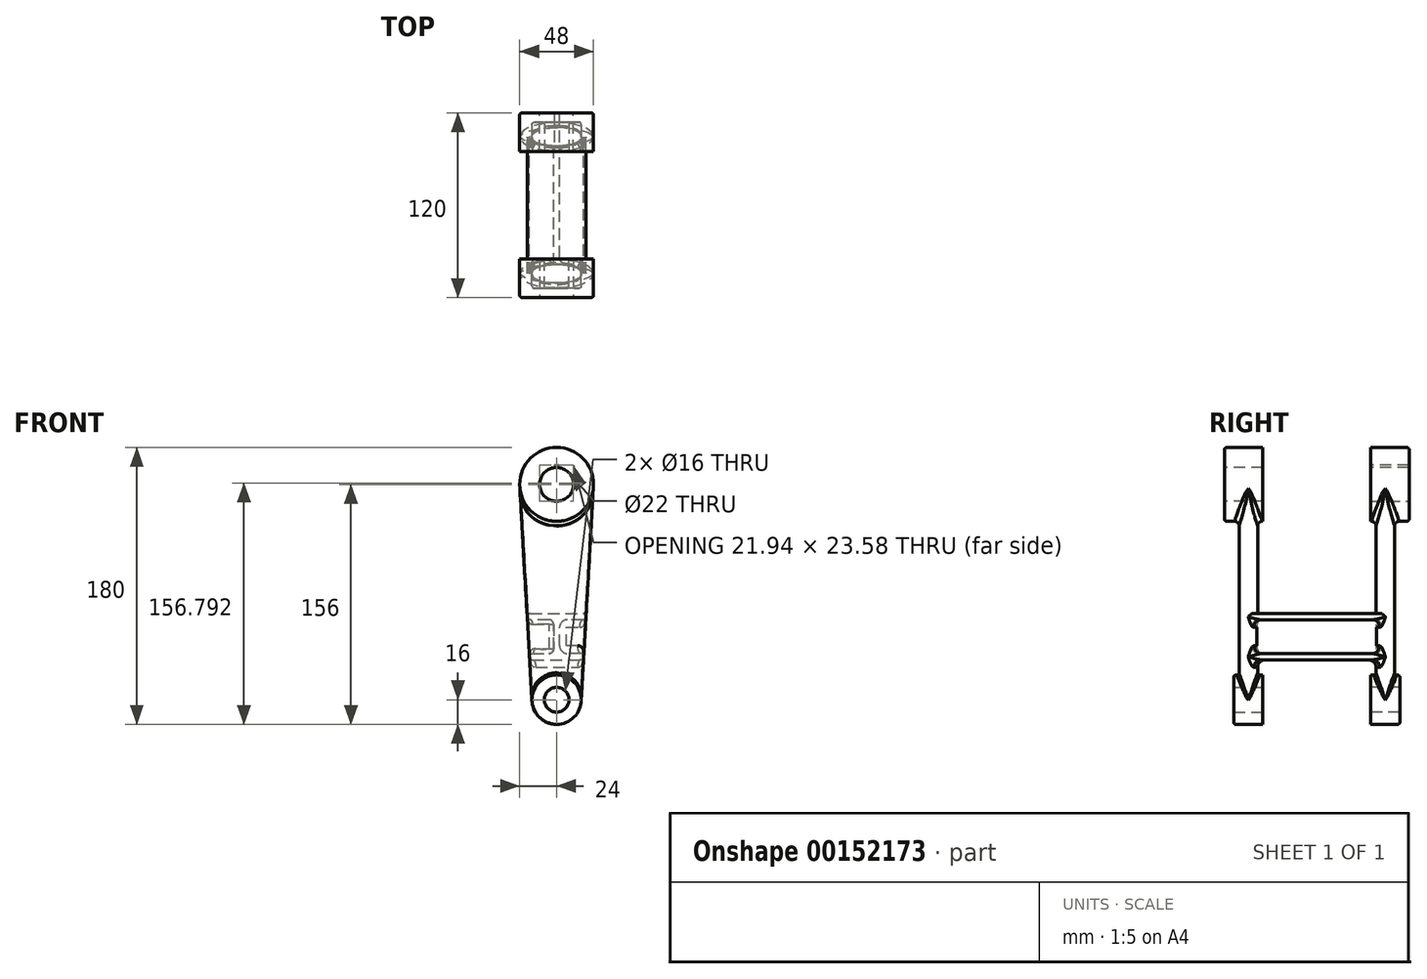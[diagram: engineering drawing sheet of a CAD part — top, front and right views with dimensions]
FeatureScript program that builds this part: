
annotation { "Feature Type Name" : "Feature", "Feature Type Description" : "" }
export const myFeature = defineFeature(function(context is Context, id is Id, definition is map)
    precondition{}
    {
        {
            var Q0;
            Q0=qCreatedBy(makeId("Front.planeOp"),FACE);
            var sketch = newSketch(context, id + "F0", { "sketchPlane" : qUnion([Q0])});
            skCircle(sketch, "E0", {"center": v(0, 140) * mm, "radius": 24 * mm});
            skCircle(sketch, "E1", {"center": v(0, 0) * mm, "radius": 16 * mm});
            skLineSegment(sketch, "E2", {"start": v(-16, 0) * mm, "end": v(-23.96, 138.62) * mm});
            skLineSegment(sketch, "E3", {"start": v(16, 0) * mm, "end": v(23.96, 138.62) * mm});
            skLineSegment(sketch, "E4", {"start": v(-23.96, 138.62) * mm, "end": v(23.96, 138.62) * mm, "construction": true});
            skSolve(sketch);
        }
        {
            var Q0;
            {var subQ0=sQuery(id+"F0.wireOp",EDGE,"E1");var subQ1=makeQuery(id+"F0.imprint","INTERSECT",VERTEX,{"derivedFrom":[subQ0,sQuery(id+"F0.wireOp",EDGE,"E2")]});Q0=makeQuery(id+"F0.imprint","IMPRINT",FACE,{"disambiguationData":[TD([[makeQuery(id+"F0.imprint","IMPRINT",EDGE,{"disambiguationData":[TD([[subQ1,1.0]])],"derivedFrom":subQ0}),1.0]])]});}
            extrude(context, id + "F1", {"entities" : qUnion([Q0]), "depth" : 19 * mm});
        }
        {
            var Q0;
            {var subQ0=sQuery(id+"F0.wireOp",EDGE,"E0");var subQ1=makeQuery(id+"F0.imprint","INTERSECT",VERTEX,{"derivedFrom":[subQ0,sQuery(id+"F0.wireOp",EDGE,"E2")]});Q0=makeQuery(id+"F0.imprint","IMPRINT",FACE,{"disambiguationData":[TD([[makeQuery(id+"F0.imprint","IMPRINT",EDGE,{"disambiguationData":[TD([[subQ1,-1.0]])],"derivedFrom":subQ0}),1.0]])]});}
            extrude(context, id + "F2", {"entities" : qUnion([Q0]), "depth" : 25 * mm});
        }
        {
            var Q0;
            Q0=qCreatedBy(makeId("Top.planeOp"),FACE);
            var sketch = newSketch(context, id + "F3", { "sketchPlane" : qUnion([Q0])});
            skEllipse(sketch, "E5", {"center": v(0, -9.5) * mm, "majorRadius": 16 * mm, "minorRadius": 6 * mm, "majorAxis": v(1, 0)});
            skSolve(sketch);
        }
        {
            var Q0;
            Q0=qCreatedBy(makeId("Top.planeOp"),FACE);
            var Q1;
            Q1=sQuery(id+"F0.wireOp",VERTEX,"E0.center");
            cPlane(context, id + "F4", {"entities" : qUnion([Q0, Q1]), "cplaneType" : CPlaneType.PLANE_POINT, "offset" : 25 * mm, "width" : 150 * mm, "height" : 150 * mm});
        }
        {
            var Q0;
            Q0=qCreatedBy(id+"F4.planeOp",FACE);
            var sketch = newSketch(context, id + "F5", { "sketchPlane" : qUnion([Q0])});
            skLineSegment(sketch, "E6", {"start": v(0, 0) * mm, "end": v(0, -9.5) * mm, "construction": true});
            skEllipse(sketch, "E7", {"center": v(0, -9.5) * mm, "majorRadius": 24 * mm, "minorRadius": 6 * mm, "majorAxis": v(1, 0)});
            skSolve(sketch);
        }
        {
            var Q0;
            Q0=qSketchRegion(id+"F5",true);
            var Q1;
            Q1=qSketchRegion(id+"F3",true);
            loft(context, id + "F6", {"operationType" : NewBodyOperationType.ADD, "sheetProfilesArray" : [{ "sheetProfileEntities" : qUnion([Q0]) }, { "sheetProfileEntities" : qUnion([Q1]) }]});
        }
        {
            var Q0;
            Q0=makeQuery(id+"F2.opExtrude","CAP_FACE",FACE,{"disambiguationData":[OSD([sQuery(id+"F0.wireOp",EDGE,"E0")])],"isStart":false});
            var sketch = newSketch(context, id + "F7", { "sketchPlane" : qUnion([Q0])});
            skCircle(sketch, "E8", {"center": v(0, 140) * mm, "radius": 11 * mm});
            skSolve(sketch);
        }
        {
            var Q0;
            Q0=qSketchRegion(id+"F7",true);
            extrude(context, id + "F8", {"entities" : qUnion([Q0]), "operationType" : NewBodyOperationType.REMOVE, "endBound" : BoundingType.THROUGH_ALL, "oppositeDirection" : true, "depth" : 25 * mm});
        }
        {
            var Q0;
            {var subQ0=sQuery(id+"F0.wireOp",EDGE,"E1");var subQ1=makeQuery(id+"F0.imprint","INTERSECT",VERTEX,{"derivedFrom":[subQ0,sQuery(id+"F0.wireOp",EDGE,"E2")]});Q0=makeQuery(id+"F0.imprint","IMPRINT",FACE,{"disambiguationData":[TD([[makeQuery(id+"F0.imprint","IMPRINT",EDGE,{"disambiguationData":[TD([[subQ1,1.0]])],"derivedFrom":subQ0}),1.0]])]});}
            var sketch = newSketch(context, id + "F9", { "sketchPlane" : qUnion([Q0])});
            skCircle(sketch, "E9", {"center": v(0, 0) * mm, "radius": 8 * mm});
            skSolve(sketch);
        }
        {
            var Q0;
            Q0=qSketchRegion(id+"F9",true);
            extrude(context, id + "F10", {"entities" : qUnion([Q0]), "operationType" : NewBodyOperationType.REMOVE, "endBound" : BoundingType.THROUGH_ALL, "depth" : 25 * mm});
        }
        {
            var Q0;
            Q0=qCreatedBy(makeId("Front.planeOp"),FACE);
            var sketch = newSketch(context, id + "F11", { "sketchPlane" : qUnion([Q0])});
            skCircle(sketch, "E10", {"center": v(0, 0) * mm, "radius": 16 * mm, "construction": true});
            skLineSegment(sketch, "E11", {"start": v(-16, 0) * mm, "end": v(-23.96, 138.62) * mm, "construction": true});
            skLineSegment(sketch, "E12", {"start": v(23.96, 138.62) * mm, "end": v(16.03, 0) * mm, "construction": true});
            skCircle(sketch, "E13", {"center": v(0, 140) * mm, "radius": 24 * mm, "construction": true});
            skLineSegment(sketch, "E14", {"start": v(0, 0) * mm, "end": v(0, 26) * mm, "construction": true});
            skLineSegment(sketch, "E15", {"start": v(0, 26) * mm, "end": v(-17.5, 26) * mm});
            skLineSegment(sketch, "E16", {"start": v(-17.5, 26) * mm, "end": v(-17.72, 30) * mm});
            skLineSegment(sketch, "E17", {"start": v(-17.72, 30) * mm, "end": v(-1.99, 30) * mm});
            skLineSegment(sketch, "E18", {"start": v(-1.99, 30) * mm, "end": v(-1.99, 52) * mm});
            skLineSegment(sketch, "E19", {"start": v(-1.99, 52) * mm, "end": v(-18.99, 52) * mm});
            skLineSegment(sketch, "E20", {"start": v(-18.99, 52) * mm, "end": v(-19.22, 56) * mm});
            skLineSegment(sketch, "E21", {"start": v(-19.22, 56) * mm, "end": v(-2.97, 56) * mm});
            skLineSegment(sketch, "E22", {"start": v(-2.97, 56) * mm, "end": v(19.23, 56) * mm});
            skLineSegment(sketch, "E23", {"start": v(19.23, 56) * mm, "end": v(19, 52) * mm});
            skLineSegment(sketch, "E24", {"start": v(19, 52) * mm, "end": v(2.01, 52) * mm});
            skLineSegment(sketch, "E25", {"start": v(2.01, 52) * mm, "end": v(2.01, 30) * mm});
            skLineSegment(sketch, "E26", {"start": v(2.01, 30) * mm, "end": v(17.74, 30) * mm});
            skLineSegment(sketch, "E27", {"start": v(17.74, 30) * mm, "end": v(17.51, 26) * mm});
            skLineSegment(sketch, "E28", {"start": v(17.51, 26) * mm, "end": v(0, 26) * mm});
            skLineSegment(sketch, "E29", {"start": v(0, 26) * mm, "end": v(17.51, 26) * mm});
            skLineSegment(sketch, "E30", {"start": v(-19.22, 56) * mm, "end": v(19.23, 56) * mm});
            skSolve(sketch);
        }
        {
            var Q0;
            Q0=sQuery(id+"F3.wireOp",VERTEX,"E5.center");
            var Q1;
            Q1=qCreatedBy(makeId("Front.planeOp"),FACE);
            cPlane(context, id + "F12", {"entities" : qUnion([Q0, Q1]), "cplaneType" : CPlaneType.PLANE_POINT, "offset" : 25 * mm, "width" : 150 * mm, "height" : 150 * mm});
        }
        {
            var Q0;
            Q0=qSketchRegion(id+"F11",true);
            var Q1;
            Q1=qCreatedBy(id+"F12.planeOp",FACE);
            var Q2;
            Q2=makeQuery(id+"F1.opExtrude","SWEPT_BODY",BODY,{"disambiguationData":[OSD([sQuery(id+"F0.wireOp",EDGE,"E1")])]});
            extrude(context, id + "F13", {"entities" : qUnion([Q0]), "operationType" : NewBodyOperationType.ADD, "endBound" : BoundingType.UP_TO_SURFACE, "endBoundEntityFace" : qUnion([Q1]), "endBoundEntityBody" : qUnion([Q2]), "depth" : 25 * mm});
        }
        {
            var Q0;
            Q0=qSketchRegion(id+"F11",true);
            extrude(context, id + "F14", {"entities" : qUnion([Q0]), "operationType" : NewBodyOperationType.ADD, "oppositeDirection" : true, "depth" : 35 * mm});
        }
        {
            var Q0;
            Q0=makeQuery(id+"F14.opExtrude","CAP_VERTEX",VERTEX,{"disambiguationData":[OSD([sQuery(id+"F11.wireOp",EDGE,"E24"),sQuery(id+"F11.wireOp",EDGE,"E25")])],"isStart":false});
            var Q1;
            Q1=qCreatedBy(makeId("Front.planeOp"),FACE);
            cPlane(context, id + "F15", {"entities" : qUnion([Q0, Q1]), "cplaneType" : CPlaneType.PLANE_POINT, "offset" : 25 * mm, "width" : 150 * mm, "height" : 150 * mm});
        }
        {
            var Q0;
            Q0=makeQuery(id+"F1.opExtrude","SWEPT_BODY",BODY,{"disambiguationData":[OSD([sQuery(id+"F0.wireOp",EDGE,"E1")])]});
            var Q1;
            Q1=qCreatedBy(id+"F15.planeOp",FACE);
            mirror(context, id + "F16", {"operationType" : NewBodyOperationType.ADD, "entities" : qUnion([Q0]), "mirrorPlane" : qUnion([Q1])});
        }
        {
            var Q0;
            {var subQ0=sQuery(id+"F11.wireOp",EDGE,"E30");var subQ1=sQuery(id+"F11.wireOp",EDGE,"E23");var subQ2=makeQuery(id+"F14.boolean.opBoolean","MERGE",EDGE,{"derivedFrom":[makeQuery(id+"F13.opExtrude","SWEPT_EDGE",EDGE,{"disambiguationData":[OSD([subQ1,subQ0])]}),makeQuery(id+"F14.opExtrude","SWEPT_EDGE",EDGE,{"disambiguationData":[OSD([subQ1,subQ0])]})]});Q0=makeQuery(id+"F16.boolean.opBoolean","MERGE",EDGE,{"derivedFrom":[subQ2,makeQuery(id+"F16.opPattern","COPY",EDGE,{"derivedFrom":subQ2,"instanceName":"1"})]});}
            var Q1;
            {var subQ0=sQuery(id+"F11.wireOp",EDGE,"E24");var subQ1=sQuery(id+"F11.wireOp",EDGE,"E23");var subQ2=makeQuery(id+"F14.boolean.opBoolean","MERGE",EDGE,{"derivedFrom":[makeQuery(id+"F13.opExtrude","SWEPT_EDGE",EDGE,{"disambiguationData":[OSD([subQ1,subQ0])]}),makeQuery(id+"F14.opExtrude","SWEPT_EDGE",EDGE,{"disambiguationData":[OSD([subQ1,subQ0])]})]});Q1=makeQuery(id+"F16.boolean.opBoolean","MERGE",EDGE,{"derivedFrom":[subQ2,makeQuery(id+"F16.opPattern","COPY",EDGE,{"derivedFrom":subQ2,"instanceName":"1"})]});}
            var Q2;
            {var subQ0=sQuery(id+"F11.wireOp",EDGE,"E27");var subQ1=sQuery(id+"F11.wireOp",EDGE,"E26");var subQ2=makeQuery(id+"F14.boolean.opBoolean","MERGE",EDGE,{"derivedFrom":[makeQuery(id+"F13.opExtrude","SWEPT_EDGE",EDGE,{"disambiguationData":[OSD([subQ1,subQ0])]}),makeQuery(id+"F14.opExtrude","SWEPT_EDGE",EDGE,{"disambiguationData":[OSD([subQ1,subQ0])]})]});Q2=makeQuery(id+"F16.boolean.opBoolean","MERGE",EDGE,{"derivedFrom":[subQ2,makeQuery(id+"F16.opPattern","COPY",EDGE,{"derivedFrom":subQ2,"instanceName":"1"})]});}
            var Q3;
            {var subQ0=sQuery(id+"F11.wireOp",EDGE,"E29");var subQ1=sQuery(id+"F11.wireOp",EDGE,"E27");var subQ2=makeQuery(id+"F14.boolean.opBoolean","MERGE",EDGE,{"derivedFrom":[makeQuery(id+"F13.opExtrude","SWEPT_EDGE",EDGE,{"disambiguationData":[OSD([subQ1,subQ0])]}),makeQuery(id+"F14.opExtrude","SWEPT_EDGE",EDGE,{"disambiguationData":[OSD([subQ1,subQ0])]})]});Q3=makeQuery(id+"F16.boolean.opBoolean","MERGE",EDGE,{"derivedFrom":[subQ2,makeQuery(id+"F16.opPattern","COPY",EDGE,{"derivedFrom":subQ2,"instanceName":"1"})]});}
            var Q4;
            {var subQ0=sQuery(id+"F11.wireOp",EDGE,"E30");var subQ1=sQuery(id+"F11.wireOp",EDGE,"E20");var subQ2=makeQuery(id+"F14.boolean.opBoolean","MERGE",EDGE,{"derivedFrom":[makeQuery(id+"F13.opExtrude","SWEPT_EDGE",EDGE,{"disambiguationData":[OSD([subQ1,subQ0])]}),makeQuery(id+"F14.opExtrude","SWEPT_EDGE",EDGE,{"disambiguationData":[OSD([subQ1,subQ0])]})]});Q4=makeQuery(id+"F16.boolean.opBoolean","MERGE",EDGE,{"derivedFrom":[subQ2,makeQuery(id+"F16.opPattern","COPY",EDGE,{"derivedFrom":subQ2,"instanceName":"1"})]});}
            var Q5;
            {var subQ0=sQuery(id+"F11.wireOp",EDGE,"E20");var subQ1=sQuery(id+"F11.wireOp",EDGE,"E19");var subQ2=makeQuery(id+"F14.boolean.opBoolean","MERGE",EDGE,{"derivedFrom":[makeQuery(id+"F13.opExtrude","SWEPT_EDGE",EDGE,{"disambiguationData":[OSD([subQ1,subQ0])]}),makeQuery(id+"F14.opExtrude","SWEPT_EDGE",EDGE,{"disambiguationData":[OSD([subQ1,subQ0])]})]});Q5=makeQuery(id+"F16.boolean.opBoolean","MERGE",EDGE,{"derivedFrom":[subQ2,makeQuery(id+"F16.opPattern","COPY",EDGE,{"derivedFrom":subQ2,"instanceName":"1"})]});}
            var Q6;
            {var subQ0=sQuery(id+"F11.wireOp",EDGE,"E17");var subQ1=sQuery(id+"F11.wireOp",EDGE,"E16");var subQ2=makeQuery(id+"F14.boolean.opBoolean","MERGE",EDGE,{"derivedFrom":[makeQuery(id+"F13.opExtrude","SWEPT_EDGE",EDGE,{"disambiguationData":[OSD([subQ1,subQ0])]}),makeQuery(id+"F14.opExtrude","SWEPT_EDGE",EDGE,{"disambiguationData":[OSD([subQ1,subQ0])]})]});Q6=makeQuery(id+"F16.boolean.opBoolean","MERGE",EDGE,{"derivedFrom":[subQ2,makeQuery(id+"F16.opPattern","COPY",EDGE,{"derivedFrom":subQ2,"instanceName":"1"})]});}
            var Q7;
            {var subQ0=sQuery(id+"F11.wireOp",EDGE,"E16");var subQ1=sQuery(id+"F11.wireOp",EDGE,"E15");var subQ2=makeQuery(id+"F14.boolean.opBoolean","MERGE",EDGE,{"derivedFrom":[makeQuery(id+"F13.opExtrude","SWEPT_EDGE",EDGE,{"disambiguationData":[OSD([subQ1,subQ0])]}),makeQuery(id+"F14.opExtrude","SWEPT_EDGE",EDGE,{"disambiguationData":[OSD([subQ1,subQ0])]})]});Q7=makeQuery(id+"F16.boolean.opBoolean","MERGE",EDGE,{"derivedFrom":[subQ2,makeQuery(id+"F16.opPattern","COPY",EDGE,{"derivedFrom":subQ2,"instanceName":"1"})]});}
            fillet(context, id + "F17", {"entities" : qUnion([Q0, Q1, Q2, Q3, Q4, Q5, Q6, Q7]), "radius" : 2 * mm, "tangentPropagation" : true, "allowEdgeOverflow" : false});
        }
        {
            var Q0;
            Q0=makeQuery(id+"F6.boolean.opBoolean","INTERSECT",EDGE,{"derivedFrom":[makeQuery(id+"F2.opExtrude","SWEPT_FACE",FACE,{"disambiguationData":[OSD([sQuery(id+"F0.wireOp",EDGE,"E0")])]}),makeQuery(id+"F6.opLoft","SWEPT_FACE",FACE,{"disambiguationData":[OSD([sQuery(id+"F3.wireOp",EDGE,"E5"),sQuery(id+"F5.wireOp",EDGE,"E7")])]})]});
            var Q1;
            Q1=makeQuery(id+"F16.opPattern","COPY",EDGE,{"derivedFrom":makeQuery(id+"F6.boolean.opBoolean","INTERSECT",EDGE,{"derivedFrom":[makeQuery(id+"F2.opExtrude","SWEPT_FACE",FACE,{"disambiguationData":[OSD([sQuery(id+"F0.wireOp",EDGE,"E0")])]}),makeQuery(id+"F6.opLoft","SWEPT_FACE",FACE,{"disambiguationData":[OSD([sQuery(id+"F3.wireOp",EDGE,"E5"),sQuery(id+"F5.wireOp",EDGE,"E7")])]})]}),"instanceName":"1"});
            fillet(context, id + "F18", {"entities" : qUnion([Q0, Q1]), "radius" : 3 * mm, "tangentPropagation" : true, "allowEdgeOverflow" : false});
        }
        {
            var Q0;
            Q0=makeQuery(id+"F13.boolean.opBoolean","INTERSECT",EDGE,{"derivedFrom":[makeQuery(id+"F6.opLoft","SWEPT_FACE",FACE,{"disambiguationData":[OSD([sQuery(id+"F3.wireOp",EDGE,"E5"),sQuery(id+"F5.wireOp",EDGE,"E7")])]}),makeQuery(id+"F13.opExtrude","SWEPT_FACE",FACE,{"disambiguationData":[OSD([sQuery(id+"F11.wireOp",EDGE,"E26")])]})]});
            var Q1;
            Q1=makeQuery(id+"F13.boolean.opBoolean","INTERSECT",EDGE,{"derivedFrom":[makeQuery(id+"F6.opLoft","SWEPT_FACE",FACE,{"disambiguationData":[OSD([sQuery(id+"F3.wireOp",EDGE,"E5"),sQuery(id+"F5.wireOp",EDGE,"E7")])]}),makeQuery(id+"F13.opExtrude","SWEPT_FACE",FACE,{"disambiguationData":[OSD([sQuery(id+"F11.wireOp",EDGE,"E25")])]})]});
            var Q2;
            Q2=makeQuery(id+"F16.opPattern","COPY",EDGE,{"derivedFrom":makeQuery(id+"F13.boolean.opBoolean","INTERSECT",EDGE,{"derivedFrom":[makeQuery(id+"F6.opLoft","SWEPT_FACE",FACE,{"disambiguationData":[OSD([sQuery(id+"F3.wireOp",EDGE,"E5"),sQuery(id+"F5.wireOp",EDGE,"E7")])]}),makeQuery(id+"F13.opExtrude","SWEPT_FACE",FACE,{"disambiguationData":[OSD([sQuery(id+"F11.wireOp",EDGE,"E26")])]})]}),"instanceName":"1"});
            var Q3;
            {var subQ0=sQuery(id+"F11.wireOp",EDGE,"E26");var subQ1=sQuery(id+"F11.wireOp",EDGE,"E25");var subQ2=makeQuery(id+"F14.boolean.opBoolean","MERGE",EDGE,{"derivedFrom":[makeQuery(id+"F13.opExtrude","SWEPT_EDGE",EDGE,{"disambiguationData":[OSD([subQ1,subQ0])]}),makeQuery(id+"F14.opExtrude","SWEPT_EDGE",EDGE,{"disambiguationData":[OSD([subQ1,subQ0])]})]});Q3=makeQuery(id+"F16.boolean.opBoolean","MERGE",EDGE,{"derivedFrom":[subQ2,makeQuery(id+"F16.opPattern","COPY",EDGE,{"derivedFrom":subQ2,"instanceName":"1"})]});}
            var Q4;
            Q4=makeQuery(id+"F16.opPattern","COPY",EDGE,{"derivedFrom":makeQuery(id+"F13.boolean.opBoolean","INTERSECT",EDGE,{"derivedFrom":[makeQuery(id+"F6.opLoft","SWEPT_FACE",FACE,{"disambiguationData":[OSD([sQuery(id+"F3.wireOp",EDGE,"E5"),sQuery(id+"F5.wireOp",EDGE,"E7")])]}),makeQuery(id+"F13.opExtrude","SWEPT_FACE",FACE,{"disambiguationData":[OSD([sQuery(id+"F11.wireOp",EDGE,"E25")])]})]}),"instanceName":"1"});
            var Q5;
            Q5=makeQuery(id+"F16.opPattern","COPY",EDGE,{"derivedFrom":makeQuery(id+"F13.boolean.opBoolean","INTERSECT",EDGE,{"derivedFrom":[makeQuery(id+"F6.opLoft","SWEPT_FACE",FACE,{"disambiguationData":[OSD([sQuery(id+"F3.wireOp",EDGE,"E5"),sQuery(id+"F5.wireOp",EDGE,"E7")])]}),makeQuery(id+"F13.opExtrude","SWEPT_FACE",FACE,{"disambiguationData":[OSD([sQuery(id+"F11.wireOp",EDGE,"E24")])]})]}),"instanceName":"1"});
            var Q6;
            {var subQ0=sQuery(id+"F11.wireOp",EDGE,"E25");var subQ1=sQuery(id+"F11.wireOp",EDGE,"E24");var subQ2=makeQuery(id+"F14.boolean.opBoolean","MERGE",EDGE,{"derivedFrom":[makeQuery(id+"F13.opExtrude","SWEPT_EDGE",EDGE,{"disambiguationData":[OSD([subQ1,subQ0])]}),makeQuery(id+"F14.opExtrude","SWEPT_EDGE",EDGE,{"disambiguationData":[OSD([subQ1,subQ0])]})]});Q6=makeQuery(id+"F16.boolean.opBoolean","MERGE",EDGE,{"derivedFrom":[subQ2,makeQuery(id+"F16.opPattern","COPY",EDGE,{"derivedFrom":subQ2,"instanceName":"1"})]});}
            var Q7;
            Q7=makeQuery(id+"F13.boolean.opBoolean","INTERSECT",EDGE,{"derivedFrom":[makeQuery(id+"F6.opLoft","SWEPT_FACE",FACE,{"disambiguationData":[OSD([sQuery(id+"F3.wireOp",EDGE,"E5"),sQuery(id+"F5.wireOp",EDGE,"E7")])]}),makeQuery(id+"F13.opExtrude","SWEPT_FACE",FACE,{"disambiguationData":[OSD([sQuery(id+"F11.wireOp",EDGE,"E24")])]})]});
            var Q8;
            Q8=makeQuery(id+"F13.boolean.opBoolean","INTERSECT",EDGE,{"derivedFrom":[makeQuery(id+"F6.opLoft","SWEPT_FACE",FACE,{"disambiguationData":[OSD([sQuery(id+"F3.wireOp",EDGE,"E5"),sQuery(id+"F5.wireOp",EDGE,"E7")])]}),makeQuery(id+"F13.opExtrude","SWEPT_FACE",FACE,{"disambiguationData":[OSD([sQuery(id+"F11.wireOp",EDGE,"E15"),sQuery(id+"F11.wireOp",EDGE,"E29")])]})]});
            var Q9;
            Q9=makeQuery(id+"F16.opPattern","COPY",EDGE,{"derivedFrom":makeQuery(id+"F13.boolean.opBoolean","INTERSECT",EDGE,{"derivedFrom":[makeQuery(id+"F6.opLoft","SWEPT_FACE",FACE,{"disambiguationData":[OSD([sQuery(id+"F3.wireOp",EDGE,"E5"),sQuery(id+"F5.wireOp",EDGE,"E7")])]}),makeQuery(id+"F13.opExtrude","SWEPT_FACE",FACE,{"disambiguationData":[OSD([sQuery(id+"F11.wireOp",EDGE,"E15"),sQuery(id+"F11.wireOp",EDGE,"E29")])]})]}),"instanceName":"1"});
            var Q10;
            Q10=makeQuery(id+"F16.opPattern","COPY",EDGE,{"derivedFrom":makeQuery(id+"F13.boolean.opBoolean","INTERSECT",EDGE,{"derivedFrom":[makeQuery(id+"F6.opLoft","SWEPT_FACE",FACE,{"disambiguationData":[OSD([sQuery(id+"F3.wireOp",EDGE,"E5"),sQuery(id+"F5.wireOp",EDGE,"E7")])]}),makeQuery(id+"F13.opExtrude","SWEPT_FACE",FACE,{"disambiguationData":[OSD([sQuery(id+"F11.wireOp",EDGE,"E30")])]})]}),"instanceName":"1"});
            var Q11;
            Q11=makeQuery(id+"F13.boolean.opBoolean","INTERSECT",EDGE,{"derivedFrom":[makeQuery(id+"F6.opLoft","SWEPT_FACE",FACE,{"disambiguationData":[OSD([sQuery(id+"F3.wireOp",EDGE,"E5"),sQuery(id+"F5.wireOp",EDGE,"E7")])]}),makeQuery(id+"F13.opExtrude","SWEPT_FACE",FACE,{"disambiguationData":[OSD([sQuery(id+"F11.wireOp",EDGE,"E30")])]})]});
            fillet(context, id + "F19", {"entities" : qUnion([Q0, Q1, Q2, Q3, Q4, Q5, Q6, Q7, Q8, Q9, Q10, Q11]), "radius" : 5 * mm, "tangentPropagation" : true, "allowEdgeOverflow" : false});
        }
        {
            var Q0;
            Q0=makeQuery(id+"F16.opPattern","COPY",EDGE,{"derivedFrom":makeQuery(id+"F6.boolean.opBoolean","INTERSECT",EDGE,{"derivedFrom":[makeQuery(id+"F1.opExtrude","SWEPT_FACE",FACE,{"disambiguationData":[OSD([sQuery(id+"F0.wireOp",EDGE,"E1")])]}),makeQuery(id+"F6.opLoft","SWEPT_FACE",FACE,{"disambiguationData":[OSD([sQuery(id+"F3.wireOp",EDGE,"E5"),sQuery(id+"F5.wireOp",EDGE,"E7")])]})]}),"instanceName":"1"});
            var Q1;
            Q1=makeQuery(id+"F6.boolean.opBoolean","INTERSECT",EDGE,{"derivedFrom":[makeQuery(id+"F1.opExtrude","SWEPT_FACE",FACE,{"disambiguationData":[OSD([sQuery(id+"F0.wireOp",EDGE,"E1")])]}),makeQuery(id+"F6.opLoft","SWEPT_FACE",FACE,{"disambiguationData":[OSD([sQuery(id+"F3.wireOp",EDGE,"E5"),sQuery(id+"F5.wireOp",EDGE,"E7")])]})]});
            fillet(context, id + "F20", {"entities" : qUnion([Q0, Q1]), "radius" : 1.5 * mm, "tangentPropagation" : true, "allowEdgeOverflow" : false});
        }
        {
            var Q0;
            Q0=makeQuery(id+"F16.opPattern","COPY",EDGE,{"derivedFrom":makeQuery(id+"F13.boolean.opBoolean","INTERSECT",EDGE,{"derivedFrom":[makeQuery(id+"F6.opLoft","SWEPT_FACE",FACE,{"disambiguationData":[OSD([sQuery(id+"F3.wireOp",EDGE,"E5"),sQuery(id+"F5.wireOp",EDGE,"E7")])]}),makeQuery(id+"F13.opExtrude","SWEPT_FACE",FACE,{"disambiguationData":[OSD([sQuery(id+"F11.wireOp",EDGE,"E19")])]})]}),"instanceName":"1"});
            var Q1;
            Q1=makeQuery(id+"F16.opPattern","COPY",EDGE,{"derivedFrom":makeQuery(id+"F13.boolean.opBoolean","INTERSECT",EDGE,{"derivedFrom":[makeQuery(id+"F6.opLoft","SWEPT_FACE",FACE,{"disambiguationData":[OSD([sQuery(id+"F3.wireOp",EDGE,"E5"),sQuery(id+"F5.wireOp",EDGE,"E7")])]}),makeQuery(id+"F13.opExtrude","SWEPT_FACE",FACE,{"disambiguationData":[OSD([sQuery(id+"F11.wireOp",EDGE,"E18")])]})]}),"instanceName":"1"});
            var Q2;
            {var subQ0=sQuery(id+"F11.wireOp",EDGE,"E19");var subQ1=sQuery(id+"F11.wireOp",EDGE,"E18");var subQ2=makeQuery(id+"F14.boolean.opBoolean","MERGE",EDGE,{"derivedFrom":[makeQuery(id+"F13.opExtrude","SWEPT_EDGE",EDGE,{"disambiguationData":[OSD([subQ1,subQ0])]}),makeQuery(id+"F14.opExtrude","SWEPT_EDGE",EDGE,{"disambiguationData":[OSD([subQ1,subQ0])]})]});Q2=makeQuery(id+"F16.boolean.opBoolean","MERGE",EDGE,{"derivedFrom":[subQ2,makeQuery(id+"F16.opPattern","COPY",EDGE,{"derivedFrom":subQ2,"instanceName":"1"})]});}
            var Q3;
            Q3=makeQuery(id+"F16.opPattern","COPY",EDGE,{"derivedFrom":makeQuery(id+"F13.boolean.opBoolean","INTERSECT",EDGE,{"derivedFrom":[makeQuery(id+"F6.opLoft","SWEPT_FACE",FACE,{"disambiguationData":[OSD([sQuery(id+"F3.wireOp",EDGE,"E5"),sQuery(id+"F5.wireOp",EDGE,"E7")])]}),makeQuery(id+"F13.opExtrude","SWEPT_FACE",FACE,{"disambiguationData":[OSD([sQuery(id+"F11.wireOp",EDGE,"E17")])]})]}),"instanceName":"1"});
            var Q4;
            {var subQ0=sQuery(id+"F11.wireOp",EDGE,"E18");var subQ1=sQuery(id+"F11.wireOp",EDGE,"E17");var subQ2=makeQuery(id+"F14.boolean.opBoolean","MERGE",EDGE,{"derivedFrom":[makeQuery(id+"F13.opExtrude","SWEPT_EDGE",EDGE,{"disambiguationData":[OSD([subQ1,subQ0])]}),makeQuery(id+"F14.opExtrude","SWEPT_EDGE",EDGE,{"disambiguationData":[OSD([subQ1,subQ0])]})]});Q4=makeQuery(id+"F16.boolean.opBoolean","MERGE",EDGE,{"derivedFrom":[subQ2,makeQuery(id+"F16.opPattern","COPY",EDGE,{"derivedFrom":subQ2,"instanceName":"1"})]});}
            var Q5;
            Q5=makeQuery(id+"F13.boolean.opBoolean","INTERSECT",EDGE,{"derivedFrom":[makeQuery(id+"F6.opLoft","SWEPT_FACE",FACE,{"disambiguationData":[OSD([sQuery(id+"F3.wireOp",EDGE,"E5"),sQuery(id+"F5.wireOp",EDGE,"E7")])]}),makeQuery(id+"F13.opExtrude","SWEPT_FACE",FACE,{"disambiguationData":[OSD([sQuery(id+"F11.wireOp",EDGE,"E17")])]})]});
            var Q6;
            Q6=makeQuery(id+"F13.boolean.opBoolean","INTERSECT",EDGE,{"derivedFrom":[makeQuery(id+"F6.opLoft","SWEPT_FACE",FACE,{"disambiguationData":[OSD([sQuery(id+"F3.wireOp",EDGE,"E5"),sQuery(id+"F5.wireOp",EDGE,"E7")])]}),makeQuery(id+"F13.opExtrude","SWEPT_FACE",FACE,{"disambiguationData":[OSD([sQuery(id+"F11.wireOp",EDGE,"E19")])]})]});
            fillet(context, id + "F21", {"entities" : qUnion([Q0, Q1, Q2, Q3, Q4, Q5, Q6]), "radius" : 3 * mm, "tangentPropagation" : true, "allowEdgeOverflow" : false});
        }
        {
            var Q0;
            Q0=makeQuery(id+"F2.opExtrude","CAP_EDGE",EDGE,{"disambiguationData":[OSD([sQuery(id+"F0.wireOp",EDGE,"E0")])],"isStart":false});
            var Q1;
            Q1=makeQuery(id+"F16.opPattern","COPY",EDGE,{"derivedFrom":makeQuery(id+"F2.opExtrude","CAP_EDGE",EDGE,{"disambiguationData":[OSD([sQuery(id+"F0.wireOp",EDGE,"E0")])],"isStart":false}),"instanceName":"1"});
            var Q2;
            Q2=makeQuery(id+"F16.opPattern","COPY",EDGE,{"derivedFrom":makeQuery(id+"F1.opExtrude","CAP_EDGE",EDGE,{"disambiguationData":[OSD([sQuery(id+"F0.wireOp",EDGE,"E1")])],"isStart":false}),"instanceName":"1"});
            var Q3;
            Q3=makeQuery(id+"F1.opExtrude","CAP_EDGE",EDGE,{"disambiguationData":[OSD([sQuery(id+"F0.wireOp",EDGE,"E1")])],"isStart":false});
            fillet(context, id + "F22", {"entities" : qUnion([Q0, Q1, Q2, Q3]), "radius" : 1.5 * mm, "tangentPropagation" : true, "allowEdgeOverflow" : false});
        }
        {
            var Q0;
            Q0=makeQuery(id+"F16.opPattern","COPY",FACE,{"derivedFrom":makeQuery(id+"F2.opExtrude","CAP_FACE",FACE,{"disambiguationData":[OSD([sQuery(id+"F0.wireOp",EDGE,"E0")])],"isStart":true}),"instanceName":"1"});
            var sketch = newSketch(context, id + "F23", { "sketchPlane" : qUnion([Q0])});
            skLineSegment(sketch, "E31", {"start": v(0, 150.88) * mm, "end": v(0, 164) * mm, "construction": true});
            skLineSegment(sketch, "E32.bottom", {"start": v(0, 150.88) * mm, "end": v(-1.6, 150.88) * mm, "construction": true});
            skLineSegment(sketch, "E32.top", {"start": v(0, 146.88) * mm, "end": v(-1.6, 146.88) * mm, "construction": true});
            skLineSegment(sketch, "E32.left", {"start": v(0, 150.88) * mm, "end": v(0, 146.88) * mm, "construction": true});
            skLineSegment(sketch, "E32.right", {"start": v(-1.6, 150.88) * mm, "end": v(-1.6, 146.88) * mm, "construction": true});
            skPoint(sketch, "E33.oppositeSnap0", {"position": v(-0.8, 146.88) * mm});
            skLineSegment(sketch, "E33.bottom", {"start": v(0, 150.88) * mm, "end": v(1.6, 150.88) * mm, "construction": true});
            skLineSegment(sketch, "E33.top", {"start": v(0, 146.88) * mm, "end": v(1.6, 146.88) * mm, "construction": true});
            skLineSegment(sketch, "E33.right", {"start": v(1.6, 150.88) * mm, "end": v(1.6, 146.88) * mm, "construction": true});
            skLineSegment(sketch, "E34.bottom", {"start": v(-1.6, 150.88) * mm, "end": v(1.6, 150.88) * mm});
            skLineSegment(sketch, "E34.top", {"start": v(-1.6, 152.58) * mm, "end": v(1.6, 152.58) * mm});
            skLineSegment(sketch, "E34.left", {"start": v(-1.6, 150.88) * mm, "end": v(-1.6, 152.58) * mm});
            skLineSegment(sketch, "E34.right", {"start": v(1.6, 150.88) * mm, "end": v(1.6, 152.58) * mm});
            skSolve(sketch);
        }
        {
            var Q0;
            Q0=makeQuery(id+"F23.imprint","IMPRINT",FACE,{"disambiguationData":[TD([[makeQuery(id+"F23.imprint","IMPRINT",EDGE,{"derivedFrom":sQuery(id+"F23.wireOp",EDGE,"E34.top")}),-1.0]])]});
            extrude(context, id + "F24", {"entities" : qUnion([Q0]), "operationType" : NewBodyOperationType.REMOVE, "endBound" : BoundingType.THROUGH_ALL, "oppositeDirection" : true, "depth" : 25 * mm});
        }
    });
